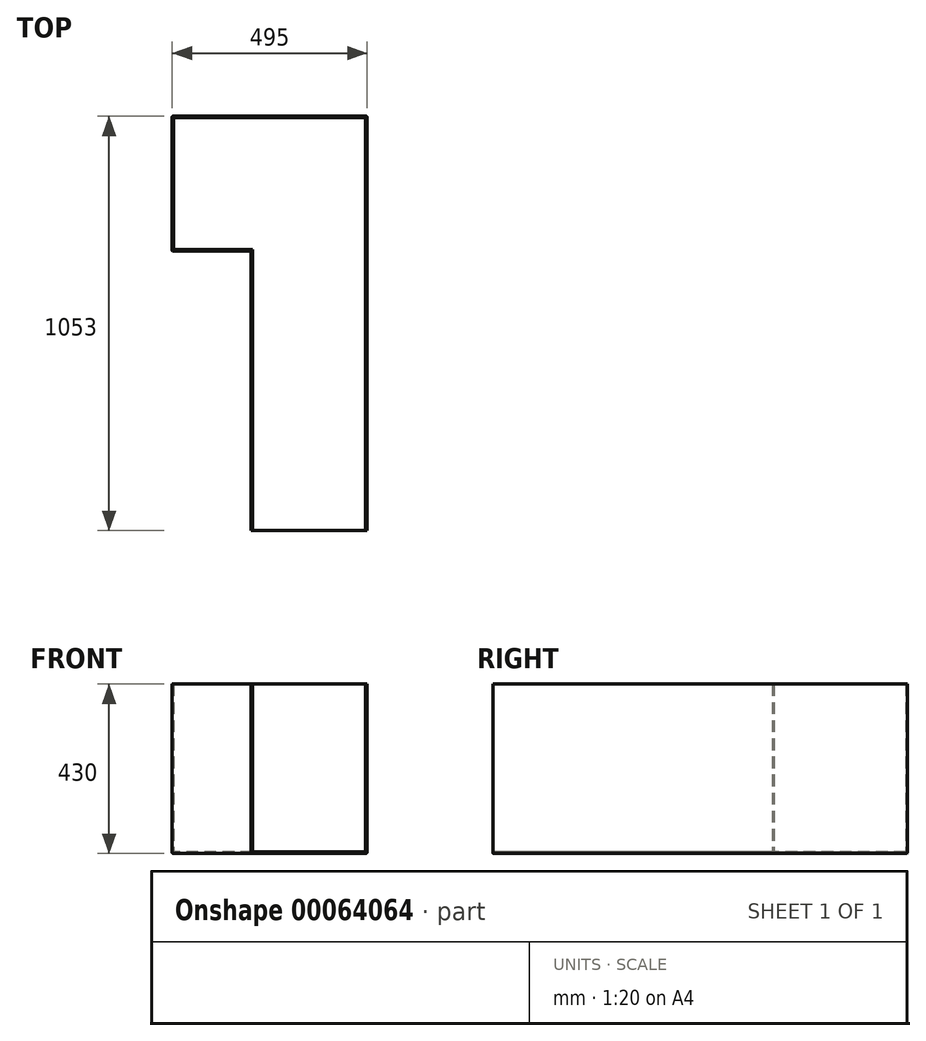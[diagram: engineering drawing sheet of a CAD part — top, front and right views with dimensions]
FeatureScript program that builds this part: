
annotation { "Feature Type Name" : "Feature", "Feature Type Description" : "" }
export const myFeature = defineFeature(function(context is Context, id is Id, definition is map)
    precondition{}
    {
        {
            var Q0;
            Q0=qCreatedBy(makeId("Top.planeOp"),FACE);
            var sketch = newSketch(context, id + "F0", { "sketchPlane" : qUnion([Q0])});
            skLineSegment(sketch, "E0", {"start": v(0, 0) * mm, "end": v(495, 0) * mm});
            skLineSegment(sketch, "E1", {"start": v(200, -343) * mm, "end": v(0, -343) * mm});
            skLineSegment(sketch, "E2", {"start": v(0, -343) * mm, "end": v(0, 0) * mm});
            skLineSegment(sketch, "E3.right", {"start": v(200, -343) * mm, "end": v(200, -1053) * mm});
            skLineSegment(sketch, "E4.left", {"start": v(495, 0) * mm, "end": v(495, -1053) * mm});
            skLineSegment(sketch, "E5.0", {"start": v(491, -4) * mm, "end": v(491, -1053) * mm});
            skLineSegment(sketch, "E5.1", {"start": v(204, -339) * mm, "end": v(204, -1053) * mm});
            skLineSegment(sketch, "E5.2", {"start": v(204, -339) * mm, "end": v(4, -339) * mm});
            skLineSegment(sketch, "E5.3", {"start": v(4, -339) * mm, "end": v(4, -4) * mm});
            skLineSegment(sketch, "E5.4", {"start": v(4, -4) * mm, "end": v(491, -4) * mm});
            skLineSegment(sketch, "E6", {"start": v(204, -1053) * mm, "end": v(200, -1053) * mm});
            skLineSegment(sketch, "E7", {"start": v(491, -1053) * mm, "end": v(495, -1053) * mm});
            skSolve(sketch);
        }
        {
            var Q0;
            Q0=makeQuery(id+"F0.imprint","IMPRINT",FACE,{"disambiguationData":[TD([[makeQuery(id+"F0.imprint","IMPRINT",EDGE,{"derivedFrom":sQuery(id+"F0.wireOp",EDGE,"E0")}),-1.0]])]});
            extrude(context, id + "F1", {"entities" : qUnion([Q0]), "depth" : 426 * mm});
        }
        {
            var Q0;
            Q0=qCreatedBy(makeId("Top.planeOp"),FACE);
            var sketch = newSketch(context, id + "F2", { "sketchPlane" : qUnion([Q0])});
            skLineSegment(sketch, "E8.0", {"start": v(200, -343) * mm, "end": v(0, -343) * mm});
            skLineSegment(sketch, "E9.0", {"start": v(0, -343) * mm, "end": v(0, 0) * mm});
            skLineSegment(sketch, "E10.0", {"start": v(0, 0) * mm, "end": v(0, 0) * mm});
            skLineSegment(sketch, "E11.0", {"start": v(0, 0) * mm, "end": v(495, 0) * mm});
            skLineSegment(sketch, "E12.0", {"start": v(200, -343) * mm, "end": v(200, -343) * mm});
            skLineSegment(sketch, "E13.0", {"start": v(495, 0) * mm, "end": v(495, 0) * mm});
            skLineSegment(sketch, "E14.0", {"start": v(495, 0) * mm, "end": v(495, -1053) * mm});
            skLineSegment(sketch, "E15", {"start": v(495, -1053) * mm, "end": v(199.99, -1053) * mm});
            skLineSegment(sketch, "E16", {"start": v(199.99, -1053) * mm, "end": v(200, -343) * mm});
            skSolve(sketch);
        }
        {
            var Q0;
            Q0=qSketchRegion(id+"F2",true);
            extrude(context, id + "F3", {"entities" : qUnion([Q0]), "operationType" : NewBodyOperationType.ADD, "oppositeDirection" : true, "depth" : 4 * mm});
        }
        {
            var Q0;
            Q0=makeQuery(id+"F3.opExtrude","CAP_EDGE",EDGE,{"disambiguationData":[OSD([sQuery(id+"F2.wireOp",EDGE,"E13.0")])],"isStart":false});
            var Q1;
            Q1=makeQuery(id+"F3.opExtrude","CAP_EDGE",EDGE,{"disambiguationData":[OSD([sQuery(id+"F2.wireOp",EDGE,"E8.0")])],"isStart":false});
            var Q2;
            Q2=makeQuery(id+"F3.opExtrude","CAP_EDGE",EDGE,{"disambiguationData":[OSD([sQuery(id+"F2.wireOp",EDGE,"E12.0")])],"isStart":false});
            var Q3;
            Q3=makeQuery(id+"F3.opExtrude","CAP_EDGE",EDGE,{"disambiguationData":[OSD([sQuery(id+"F2.wireOp",EDGE,"E9.0")])],"isStart":false});
            var Q4;
            Q4=makeQuery(id+"F3.opExtrude","CAP_EDGE",EDGE,{"disambiguationData":[OSD([sQuery(id+"F2.wireOp",EDGE,"E11.0")])],"isStart":false});
            var Q5;
            Q5=makeQuery(id+"F3.boolean.opBoolean","MERGE",EDGE,{"derivedFrom":[makeQuery(id+"F1.opExtrude","SWEPT_EDGE",EDGE,{"disambiguationData":[OSD([sQuery(id+"F0.wireOp",EDGE,"E1"),sQuery(id+"F0.wireOp",EDGE,"E3.right")])]}),makeQuery(id+"F3.opExtrude","SWEPT_EDGE",EDGE,{"disambiguationData":[OSD([sQuery(id+"F2.wireOp",EDGE,"E8.0"),sQuery(id+"F2.wireOp",EDGE,"E12.0")])]})]});
            var Q6;
            Q6=makeQuery(id+"F3.boolean.opBoolean","MERGE",EDGE,{"derivedFrom":[makeQuery(id+"F1.opExtrude","SWEPT_EDGE",EDGE,{"disambiguationData":[OSD([sQuery(id+"F0.wireOp",EDGE,"E1"),sQuery(id+"F0.wireOp",EDGE,"E2")])]}),makeQuery(id+"F3.opExtrude","SWEPT_EDGE",EDGE,{"disambiguationData":[OSD([sQuery(id+"F2.wireOp",EDGE,"E8.0"),sQuery(id+"F2.wireOp",EDGE,"E9.0")])]})]});
            var Q7;
            Q7=makeQuery(id+"F3.boolean.opBoolean","MERGE",EDGE,{"derivedFrom":[makeQuery(id+"F1.opExtrude","SWEPT_EDGE",EDGE,{"disambiguationData":[OSD([sQuery(id+"F0.wireOp",EDGE,"E0"),sQuery(id+"F0.wireOp",EDGE,"E2")])]}),makeQuery(id+"F3.opExtrude","SWEPT_EDGE",EDGE,{"disambiguationData":[OSD([sQuery(id+"F2.wireOp",EDGE,"E9.0"),sQuery(id+"F2.wireOp",EDGE,"E11.0")])]})]});
            var Q8;
            Q8=makeQuery(id+"F1.opExtrude","SWEPT_EDGE",EDGE,{"disambiguationData":[OSD([sQuery(id+"F0.wireOp",EDGE,"41269a5a-69f6-4670-b1a7-19bf830e781a"),sQuery(id+"F0.wireOp",EDGE,"E4.right")])]});
            var Q9;
            Q9=makeQuery(id+"F1.opExtrude","SWEPT_EDGE",EDGE,{"disambiguationData":[OSD([sQuery(id+"F0.wireOp",EDGE,"cc5772d9-c29a-4c81-bde5-837d5d9decb7"),sQuery(id+"F0.wireOp",EDGE,"E3.left")])]});
            var Q10;
            Q10=makeQuery(id+"F1.opExtrude","SWEPT_EDGE",EDGE,{"disambiguationData":[OSD([sQuery(id+"F0.wireOp",EDGE,"41269a5a-69f6-4670-b1a7-19bf830e781a"),sQuery(id+"F0.wireOp",EDGE,"05cfef9b-c223-4bdb-b400-77ea615546ad")])]});
            var Q11;
            Q11=makeQuery(id+"F1.opExtrude","SWEPT_EDGE",EDGE,{"disambiguationData":[OSD([sQuery(id+"F0.wireOp",EDGE,"05cfef9b-c223-4bdb-b400-77ea615546ad"),sQuery(id+"F0.wireOp",EDGE,"cc5772d9-c29a-4c81-bde5-837d5d9decb7")])]});
            var Q12;
            Q12=makeQuery(id+"F3.boolean.opBoolean","MERGE",EDGE,{"derivedFrom":[makeQuery(id+"F1.opExtrude","SWEPT_EDGE",EDGE,{"disambiguationData":[OSD([sQuery(id+"F0.wireOp",EDGE,"E0"),sQuery(id+"F0.wireOp",EDGE,"E4.left")])]}),makeQuery(id+"F3.opExtrude","SWEPT_EDGE",EDGE,{"disambiguationData":[OSD([sQuery(id+"F2.wireOp",EDGE,"E11.0"),sQuery(id+"F2.wireOp",EDGE,"E13.0")])]})]});
            var Q13;
            Q13=makeQuery(id+"F3.opExtrude","CAP_EDGE",EDGE,{"disambiguationData":[OSD([sQuery(id+"F2.wireOp",EDGE,"E16")])],"isStart":false});
            var Q14;
            Q14=makeQuery(id+"F3.opExtrude","CAP_EDGE",EDGE,{"disambiguationData":[OSD([sQuery(id+"F2.wireOp",EDGE,"E14.0")])],"isStart":false});
            fillet(context, id + "F4", {"entities" : qUnion([Q0, Q1, Q2, Q3, Q4, Q5, Q6, Q7, Q8, Q9, Q10, Q11, Q12, Q13, Q14]), "radius" : 2 * mm, "tangentPropagation" : true, "allowEdgeOverflow" : false});
        }
    });
